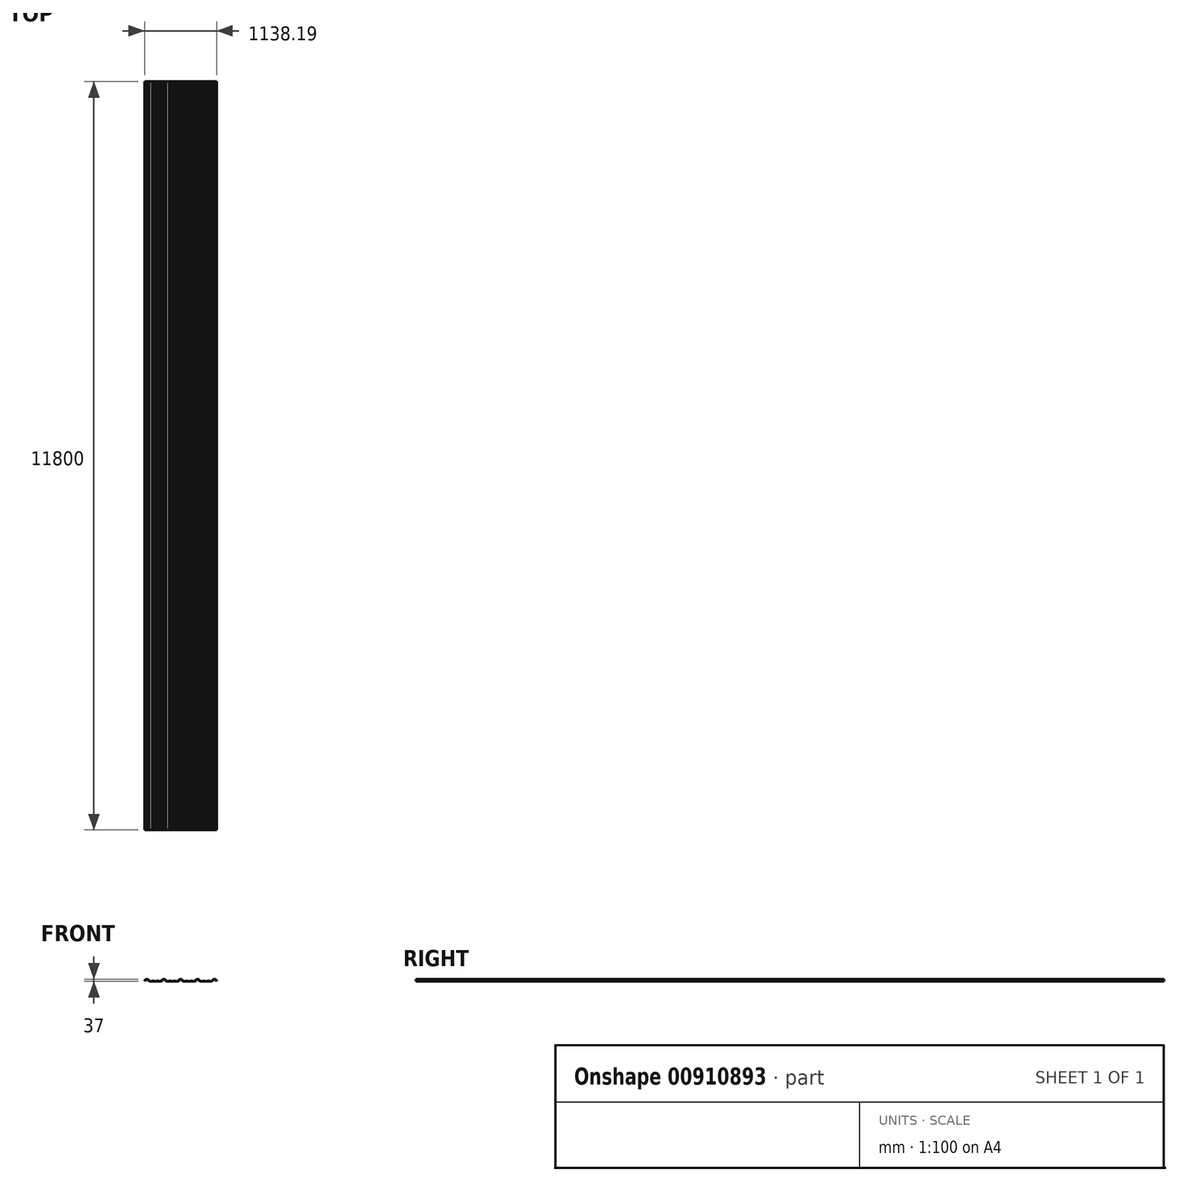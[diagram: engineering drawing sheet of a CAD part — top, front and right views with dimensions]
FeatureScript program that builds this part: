
annotation { "Feature Type Name" : "Feature", "Feature Type Description" : "" }
export const myFeature = defineFeature(function(context is Context, id is Id, definition is map)
    precondition{}
    {
        {
            var Q0;
            Q0=qCreatedBy(makeId("Front.planeOp"),FACE);
            var sketch = newSketch(context, id + "F0", { "sketchPlane" : qUnion([Q0])});
            skLineSegment(sketch, "E0.bottom", {"start": v(-37.5, 37) * mm, "end": v(37.5, 37) * mm, "construction": true});
            skLineSegment(sketch, "E0.top", {"start": v(-37.5, 0) * mm, "end": v(37.5, 0) * mm, "construction": true});
            skLineSegment(sketch, "E0.left", {"start": v(-37.5, 37) * mm, "end": v(-37.5, 0) * mm, "construction": true});
            skLineSegment(sketch, "E0.right", {"start": v(37.5, 37) * mm, "end": v(37.5, 0) * mm, "construction": true});
            skLineSegment(sketch, "E1.bottom", {"start": v(-16, 37) * mm, "end": v(16, 37) * mm, "construction": true});
            skLineSegment(sketch, "E1.top", {"start": v(-16, 0) * mm, "end": v(16, 0) * mm, "construction": true});
            skLineSegment(sketch, "E1.left", {"start": v(-16, 37) * mm, "end": v(-16, 0) * mm, "construction": true});
            skLineSegment(sketch, "E1.right", {"start": v(16, 37) * mm, "end": v(16, 0) * mm, "construction": true});
            skLineSegment(sketch, "E2.left", {"start": v(0, 37) * mm, "end": v(0, 0) * mm, "construction": true});
            skLineSegment(sketch, "E3", {"start": v(16, 37) * mm, "end": v(266, 37) * mm, "construction": true});
            skLineSegment(sketch, "E4", {"start": v(85.17, 0) * mm, "end": v(85.17, 6) * mm, "construction": true});
            skLineSegment(sketch, "E5", {"start": v(85.17, 3) * mm, "end": v(109.17, 3) * mm, "construction": true});
            skLineSegment(sketch, "E6", {"start": v(109.17, 3) * mm, "end": v(109.17, 0) * mm, "construction": true});
            skLineSegment(sketch, "E7", {"start": v(109.17, 0) * mm, "end": v(156.83, 0) * mm, "construction": true});
            skLineSegment(sketch, "E8", {"start": v(156.83, 0) * mm, "end": v(156.83, 3) * mm, "construction": true});
            skLineSegment(sketch, "E9", {"start": v(156.83, 3) * mm, "end": v(180.83, 3) * mm, "construction": true});
            skLineSegment(sketch, "E10", {"start": v(180.83, 3) * mm, "end": v(180.83, 0) * mm, "construction": true});
            skLineSegment(sketch, "E11", {"start": v(180.83, 0) * mm, "end": v(228.5, 0) * mm, "construction": true});
            skLineSegment(sketch, "E12", {"start": v(85.17, 0) * mm, "end": v(37.5, 0) * mm, "construction": true});
            skLineSegment(sketch, "E13", {"start": v(-37.5, 18.5) * mm, "end": v(37.5, 18.5) * mm, "construction": true});
            skLineSegment(sketch, "E14", {"start": v(-37.5, 3) * mm, "end": v(-28.55, 18.5) * mm, "construction": true});
            skLineSegment(sketch, "E15.0", {"start": v(-37.5, 15.5) * mm, "end": v(37.5, 15.5) * mm, "construction": true});
            skLineSegment(sketch, "E16.0", {"start": v(-37.5, 3) * mm, "end": v(37.5, 3) * mm, "construction": true});
            skLineSegment(sketch, "E17.0", {"start": v(-14.27, 34) * mm, "end": v(14.27, 34) * mm, "construction": true});
            skLineSegment(sketch, "E18.0", {"start": v(-35.77, 0) * mm, "end": v(-26.82, 15.5) * mm, "construction": true});
            skLineSegment(sketch, "E19", {"start": v(-26.68, 18.5) * mm, "end": v(-16, 37) * mm, "construction": true});
            skLineSegment(sketch, "E20.0", {"start": v(-24.95, 15.5) * mm, "end": v(-14.27, 34) * mm, "construction": true});
            skLineSegment(sketch, "E21.MirrorCS", {"start": v(37.5, 3) * mm, "end": v(28.55, 18.5) * mm, "construction": true});
            skLineSegment(sketch, "E22.MirrorCS", {"start": v(24.95, 15.5) * mm, "end": v(14.27, 34) * mm, "construction": true});
            skLineSegment(sketch, "E23.MirrorCS", {"start": v(35.77, 0) * mm, "end": v(26.82, 15.5) * mm, "construction": true});
            skLineSegment(sketch, "E24.MirrorCS", {"start": v(26.68, 18.5) * mm, "end": v(16, 37) * mm, "construction": true});
            skLineSegment(sketch, "E25.0", {"start": v(-36.7, 4.4) * mm, "end": v(-33.23, 4.4) * mm, "construction": true});
            skLineSegment(sketch, "E26.0", {"start": v(85.17, 3) * mm, "end": v(37.5, 3) * mm, "construction": true});
            skLineSegment(sketch, "E27.0", {"start": v(85.17, 6) * mm, "end": v(109.17, 6) * mm, "construction": true});
            skLineSegment(sketch, "E28.0", {"start": v(109.17, 3) * mm, "end": v(156.83, 3) * mm, "construction": true});
            skLineSegment(sketch, "E29.0", {"start": v(156.83, 6) * mm, "end": v(180.83, 6) * mm, "construction": true});
            skLineSegment(sketch, "E30.0", {"start": v(180.83, 3) * mm, "end": v(228.5, 3) * mm, "construction": true});
            skLineSegment(sketch, "E31", {"start": v(85.17, 0) * mm, "end": v(88.63, 6) * mm, "construction": true});
            skLineSegment(sketch, "E32", {"start": v(85.17, 6) * mm, "end": v(81.7, 0) * mm, "construction": true});
            skLineSegment(sketch, "E33", {"start": v(97.17, 6) * mm, "end": v(97.17, 3) * mm, "construction": true});
            skLineSegment(sketch, "E34.MirrorCS", {"start": v(109.17, 0) * mm, "end": v(105.7, 6) * mm, "construction": true});
            skLineSegment(sketch, "E35.MirrorCS", {"start": v(109.17, 6) * mm, "end": v(112.63, 0) * mm, "construction": true});
            skLineSegment(sketch, "E36", {"start": v(133, 3) * mm, "end": v(133, 0) * mm, "construction": true});
            skLineSegment(sketch, "E37.MirrorCS", {"start": v(156.83, 6) * mm, "end": v(153.37, 0) * mm, "construction": true});
            skLineSegment(sketch, "E38.MirrorCS", {"start": v(156.83, 0) * mm, "end": v(160.3, 6) * mm, "construction": true});
            skLineSegment(sketch, "E39.MirrorCS", {"start": v(168.83, 6) * mm, "end": v(168.83, 3) * mm, "construction": true});
            skLineSegment(sketch, "E40.MirrorCS", {"start": v(180.83, 0) * mm, "end": v(177.37, 6) * mm, "construction": true});
            skLineSegment(sketch, "E41.MirrorCS", {"start": v(180.83, 6) * mm, "end": v(184.3, 0) * mm, "construction": true});
            skLineSegment(sketch, "E42.1.0.0", {"start": v(228.5, 0) * mm, "end": v(303.5, 0) * mm, "construction": true});
            skLineSegment(sketch, "E42.1.0.1", {"start": v(250, 37) * mm, "end": v(250, 0) * mm, "construction": true});
            skLineSegment(sketch, "E42.1.0.2", {"start": v(292.68, 18.5) * mm, "end": v(282, 37) * mm, "construction": true});
            skLineSegment(sketch, "E42.1.0.3", {"start": v(241.05, 15.5) * mm, "end": v(251.73, 34) * mm, "construction": true});
            skLineSegment(sketch, "E42.1.0.4", {"start": v(228.5, 18.5) * mm, "end": v(303.5, 18.5) * mm, "construction": true});
            skLineSegment(sketch, "E42.1.0.5", {"start": v(303.5, 3) * mm, "end": v(294.55, 18.5) * mm, "construction": true});
            skLineSegment(sketch, "E42.1.0.6", {"start": v(228.5, 37) * mm, "end": v(303.5, 37) * mm, "construction": true});
            skLineSegment(sketch, "E42.1.0.7", {"start": v(301.77, 0) * mm, "end": v(292.82, 15.5) * mm, "construction": true});
            skLineSegment(sketch, "E42.1.0.8", {"start": v(303.5, 37) * mm, "end": v(303.5, 0) * mm, "construction": true});
            skLineSegment(sketch, "E42.1.0.9", {"start": v(446.83, 3) * mm, "end": v(494.5, 3) * mm, "construction": true});
            skLineSegment(sketch, "E42.1.0.10", {"start": v(290.95, 15.5) * mm, "end": v(280.27, 34) * mm, "construction": true});
            skLineSegment(sketch, "E42.1.0.11", {"start": v(266, 37) * mm, "end": v(266, 0) * mm, "construction": true});
            skLineSegment(sketch, "E42.1.0.12", {"start": v(250, 0) * mm, "end": v(282, 0) * mm, "construction": true});
            skLineSegment(sketch, "E42.1.0.13", {"start": v(228.5, 37) * mm, "end": v(228.5, 0) * mm, "construction": true});
            skLineSegment(sketch, "E42.1.0.14", {"start": v(228.5, 3) * mm, "end": v(303.5, 3) * mm, "construction": true});
            skLineSegment(sketch, "E42.1.0.15", {"start": v(351.17, 0) * mm, "end": v(303.5, 0) * mm, "construction": true});
            skLineSegment(sketch, "E42.1.0.16", {"start": v(351.17, 3) * mm, "end": v(303.5, 3) * mm, "construction": true});
            skLineSegment(sketch, "E42.1.0.17", {"start": v(228.5, 15.5) * mm, "end": v(303.5, 15.5) * mm, "construction": true});
            skLineSegment(sketch, "E42.1.0.18", {"start": v(282, 37) * mm, "end": v(282, 0) * mm, "construction": true});
            skLineSegment(sketch, "E42.1.0.19", {"start": v(375.17, 0) * mm, "end": v(422.83, 0) * mm, "construction": true});
            skLineSegment(sketch, "E42.1.0.20", {"start": v(446.83, 0) * mm, "end": v(494.5, 0) * mm, "construction": true});
            skLineSegment(sketch, "E42.1.0.21", {"start": v(375.17, 3) * mm, "end": v(422.83, 3) * mm, "construction": true});
            skLineSegment(sketch, "E42.1.0.22", {"start": v(250, 37) * mm, "end": v(282, 37) * mm, "construction": true});
            skLineSegment(sketch, "E42.1.0.23", {"start": v(239.32, 18.5) * mm, "end": v(250, 37) * mm, "construction": true});
            skLineSegment(sketch, "E42.1.0.24", {"start": v(351.17, 3) * mm, "end": v(375.17, 3) * mm, "construction": true});
            skLineSegment(sketch, "E42.1.0.25", {"start": v(251.73, 34) * mm, "end": v(280.27, 34) * mm, "construction": true});
            skLineSegment(sketch, "E42.1.0.26", {"start": v(228.5, 3) * mm, "end": v(237.45, 18.5) * mm, "construction": true});
            skLineSegment(sketch, "E42.1.0.27", {"start": v(351.17, 6) * mm, "end": v(375.17, 6) * mm, "construction": true});
            skLineSegment(sketch, "E42.1.0.28", {"start": v(230.23, 0) * mm, "end": v(239.18, 15.5) * mm, "construction": true});
            skLineSegment(sketch, "E42.1.0.29", {"start": v(434.83, 6) * mm, "end": v(434.83, 3) * mm, "construction": true});
            skLineSegment(sketch, "E42.1.0.30", {"start": v(363.17, 6) * mm, "end": v(363.17, 3) * mm, "construction": true});
            skLineSegment(sketch, "E42.1.0.31", {"start": v(422.83, 3) * mm, "end": v(446.83, 3) * mm, "construction": true});
            skLineSegment(sketch, "E42.1.0.32", {"start": v(229.3, 4.4) * mm, "end": v(232.77, 4.4) * mm, "construction": true});
            skLineSegment(sketch, "E42.1.0.33", {"start": v(422.83, 6) * mm, "end": v(446.83, 6) * mm, "construction": true});
            skLineSegment(sketch, "E42.1.0.34", {"start": v(399, 3) * mm, "end": v(399, 0) * mm, "construction": true});
            skLineSegment(sketch, "E42.1.0.35", {"start": v(446.83, 6) * mm, "end": v(450.3, 0) * mm, "construction": true});
            skLineSegment(sketch, "E42.1.0.36", {"start": v(422.83, 6) * mm, "end": v(419.37, 0) * mm, "construction": true});
            skLineSegment(sketch, "E42.1.0.37", {"start": v(375.17, 3) * mm, "end": v(375.17, 0) * mm, "construction": true});
            skLineSegment(sketch, "E42.1.0.38", {"start": v(446.83, 3) * mm, "end": v(446.83, 0) * mm, "construction": true});
            skLineSegment(sketch, "E42.1.0.39", {"start": v(446.83, 0) * mm, "end": v(443.37, 6) * mm, "construction": true});
            skLineSegment(sketch, "E42.1.0.40", {"start": v(375.17, 6) * mm, "end": v(378.63, 0) * mm, "construction": true});
            skLineSegment(sketch, "E42.1.0.41", {"start": v(422.83, 0) * mm, "end": v(426.3, 6) * mm, "construction": true});
            skLineSegment(sketch, "E42.1.0.42", {"start": v(375.17, 0) * mm, "end": v(371.7, 6) * mm, "construction": true});
            skLineSegment(sketch, "E42.1.0.43", {"start": v(351.17, 6) * mm, "end": v(347.7, 0) * mm, "construction": true});
            skLineSegment(sketch, "E42.1.0.44", {"start": v(422.83, 0) * mm, "end": v(422.83, 3) * mm, "construction": true});
            skLineSegment(sketch, "E42.1.0.45", {"start": v(351.17, 0) * mm, "end": v(351.17, 6) * mm, "construction": true});
            skLineSegment(sketch, "E42.1.0.46", {"start": v(351.17, 0) * mm, "end": v(354.63, 6) * mm, "construction": true});
            skLineSegment(sketch, "E42.2.0.0", {"start": v(494.5, 0) * mm, "end": v(569.5, 0) * mm, "construction": true});
            skLineSegment(sketch, "E42.2.0.1", {"start": v(516, 37) * mm, "end": v(516, 0) * mm, "construction": true});
            skLineSegment(sketch, "E42.2.0.2", {"start": v(558.68, 18.5) * mm, "end": v(548, 37) * mm, "construction": true});
            skLineSegment(sketch, "E42.2.0.3", {"start": v(507.05, 15.5) * mm, "end": v(517.73, 34) * mm, "construction": true});
            skLineSegment(sketch, "E42.2.0.4", {"start": v(494.5, 18.5) * mm, "end": v(569.5, 18.5) * mm, "construction": true});
            skLineSegment(sketch, "E42.2.0.5", {"start": v(569.5, 3) * mm, "end": v(560.55, 18.5) * mm, "construction": true});
            skLineSegment(sketch, "E42.2.0.6", {"start": v(494.5, 37) * mm, "end": v(569.5, 37) * mm, "construction": true});
            skLineSegment(sketch, "E42.2.0.7", {"start": v(567.77, 0) * mm, "end": v(558.82, 15.5) * mm, "construction": true});
            skLineSegment(sketch, "E42.2.0.8", {"start": v(569.5, 37) * mm, "end": v(569.5, 0) * mm, "construction": true});
            skLineSegment(sketch, "E42.2.0.9", {"start": v(712.83, 3) * mm, "end": v(760.5, 3) * mm, "construction": true});
            skLineSegment(sketch, "E42.2.0.10", {"start": v(556.95, 15.5) * mm, "end": v(546.27, 34) * mm, "construction": true});
            skLineSegment(sketch, "E42.2.0.11", {"start": v(532, 37) * mm, "end": v(532, 0) * mm, "construction": true});
            skLineSegment(sketch, "E42.2.0.12", {"start": v(516, 0) * mm, "end": v(548, 0) * mm, "construction": true});
            skLineSegment(sketch, "E42.2.0.13", {"start": v(494.5, 37) * mm, "end": v(494.5, 0) * mm, "construction": true});
            skLineSegment(sketch, "E42.2.0.14", {"start": v(494.5, 3) * mm, "end": v(569.5, 3) * mm, "construction": true});
            skLineSegment(sketch, "E42.2.0.15", {"start": v(617.17, 0) * mm, "end": v(569.5, 0) * mm, "construction": true});
            skLineSegment(sketch, "E42.2.0.16", {"start": v(617.17, 3) * mm, "end": v(569.5, 3) * mm, "construction": true});
            skLineSegment(sketch, "E42.2.0.17", {"start": v(494.5, 15.5) * mm, "end": v(569.5, 15.5) * mm, "construction": true});
            skLineSegment(sketch, "E42.2.0.18", {"start": v(548, 37) * mm, "end": v(548, 0) * mm, "construction": true});
            skLineSegment(sketch, "E42.2.0.19", {"start": v(641.17, 0) * mm, "end": v(688.83, 0) * mm, "construction": true});
            skLineSegment(sketch, "E42.2.0.20", {"start": v(712.83, 0) * mm, "end": v(760.5, 0) * mm, "construction": true});
            skLineSegment(sketch, "E42.2.0.21", {"start": v(641.17, 3) * mm, "end": v(688.83, 3) * mm, "construction": true});
            skLineSegment(sketch, "E42.2.0.22", {"start": v(516, 37) * mm, "end": v(548, 37) * mm, "construction": true});
            skLineSegment(sketch, "E42.2.0.23", {"start": v(505.32, 18.5) * mm, "end": v(516, 37) * mm, "construction": true});
            skLineSegment(sketch, "E42.2.0.24", {"start": v(617.17, 3) * mm, "end": v(641.17, 3) * mm, "construction": true});
            skLineSegment(sketch, "E42.2.0.25", {"start": v(517.73, 34) * mm, "end": v(546.27, 34) * mm, "construction": true});
            skLineSegment(sketch, "E42.2.0.26", {"start": v(494.5, 3) * mm, "end": v(503.45, 18.5) * mm, "construction": true});
            skLineSegment(sketch, "E42.2.0.27", {"start": v(617.17, 6) * mm, "end": v(641.17, 6) * mm, "construction": true});
            skLineSegment(sketch, "E42.2.0.28", {"start": v(496.23, 0) * mm, "end": v(505.18, 15.5) * mm, "construction": true});
            skLineSegment(sketch, "E42.2.0.29", {"start": v(700.83, 6) * mm, "end": v(700.83, 3) * mm, "construction": true});
            skLineSegment(sketch, "E42.2.0.30", {"start": v(629.17, 6) * mm, "end": v(629.17, 3) * mm, "construction": true});
            skLineSegment(sketch, "E42.2.0.31", {"start": v(688.83, 3) * mm, "end": v(712.83, 3) * mm, "construction": true});
            skLineSegment(sketch, "E42.2.0.32", {"start": v(495.3, 4.4) * mm, "end": v(498.77, 4.4) * mm, "construction": true});
            skLineSegment(sketch, "E42.2.0.33", {"start": v(688.83, 6) * mm, "end": v(712.83, 6) * mm, "construction": true});
            skLineSegment(sketch, "E42.2.0.34", {"start": v(665, 3) * mm, "end": v(665, 0) * mm, "construction": true});
            skLineSegment(sketch, "E42.2.0.35", {"start": v(712.83, 6) * mm, "end": v(716.3, 0) * mm, "construction": true});
            skLineSegment(sketch, "E42.2.0.36", {"start": v(688.83, 6) * mm, "end": v(685.37, 0) * mm, "construction": true});
            skLineSegment(sketch, "E42.2.0.37", {"start": v(641.17, 3) * mm, "end": v(641.17, 0) * mm, "construction": true});
            skLineSegment(sketch, "E42.2.0.38", {"start": v(712.83, 3) * mm, "end": v(712.83, 0) * mm, "construction": true});
            skLineSegment(sketch, "E42.2.0.39", {"start": v(712.83, 0) * mm, "end": v(709.37, 6) * mm, "construction": true});
            skLineSegment(sketch, "E42.2.0.40", {"start": v(641.17, 6) * mm, "end": v(644.63, 0) * mm, "construction": true});
            skLineSegment(sketch, "E42.2.0.41", {"start": v(688.83, 0) * mm, "end": v(692.3, 6) * mm, "construction": true});
            skLineSegment(sketch, "E42.2.0.42", {"start": v(641.17, 0) * mm, "end": v(637.7, 6) * mm, "construction": true});
            skLineSegment(sketch, "E42.2.0.43", {"start": v(617.17, 6) * mm, "end": v(613.7, 0) * mm, "construction": true});
            skLineSegment(sketch, "E42.2.0.44", {"start": v(688.83, 0) * mm, "end": v(688.83, 3) * mm, "construction": true});
            skLineSegment(sketch, "E42.2.0.45", {"start": v(617.17, 0) * mm, "end": v(617.17, 6) * mm, "construction": true});
            skLineSegment(sketch, "E42.2.0.46", {"start": v(617.17, 0) * mm, "end": v(620.63, 6) * mm, "construction": true});
            skLineSegment(sketch, "E42.3.0.0", {"start": v(760.5, 0) * mm, "end": v(835.5, 0) * mm, "construction": true});
            skLineSegment(sketch, "E42.3.0.1", {"start": v(782, 37) * mm, "end": v(782, 0) * mm, "construction": true});
            skLineSegment(sketch, "E42.3.0.2", {"start": v(824.68, 18.5) * mm, "end": v(814, 37) * mm, "construction": true});
            skLineSegment(sketch, "E42.3.0.3", {"start": v(773.05, 15.5) * mm, "end": v(783.73, 34) * mm, "construction": true});
            skLineSegment(sketch, "E42.3.0.4", {"start": v(760.5, 18.5) * mm, "end": v(835.5, 18.5) * mm, "construction": true});
            skLineSegment(sketch, "E42.3.0.5", {"start": v(835.5, 3) * mm, "end": v(826.55, 18.5) * mm, "construction": true});
            skLineSegment(sketch, "E42.3.0.6", {"start": v(760.5, 37) * mm, "end": v(835.5, 37) * mm, "construction": true});
            skLineSegment(sketch, "E42.3.0.7", {"start": v(833.77, 0) * mm, "end": v(824.82, 15.5) * mm, "construction": true});
            skLineSegment(sketch, "E42.3.0.8", {"start": v(835.5, 37) * mm, "end": v(835.5, 0) * mm, "construction": true});
            skLineSegment(sketch, "E42.3.0.9", {"start": v(978.83, 3) * mm, "end": v(1026.5, 3) * mm, "construction": true});
            skLineSegment(sketch, "E42.3.0.10", {"start": v(822.95, 15.5) * mm, "end": v(812.27, 34) * mm, "construction": true});
            skLineSegment(sketch, "E42.3.0.11", {"start": v(798, 37) * mm, "end": v(798, 0) * mm, "construction": true});
            skLineSegment(sketch, "E42.3.0.12", {"start": v(782, 0) * mm, "end": v(814, 0) * mm, "construction": true});
            skLineSegment(sketch, "E42.3.0.13", {"start": v(760.5, 37) * mm, "end": v(760.5, 0) * mm, "construction": true});
            skLineSegment(sketch, "E42.3.0.14", {"start": v(760.5, 3) * mm, "end": v(835.5, 3) * mm, "construction": true});
            skLineSegment(sketch, "E42.3.0.15", {"start": v(883.17, 0) * mm, "end": v(835.5, 0) * mm, "construction": true});
            skLineSegment(sketch, "E42.3.0.16", {"start": v(883.17, 3) * mm, "end": v(835.5, 3) * mm, "construction": true});
            skLineSegment(sketch, "E42.3.0.17", {"start": v(760.5, 15.5) * mm, "end": v(835.5, 15.5) * mm, "construction": true});
            skLineSegment(sketch, "E42.3.0.18", {"start": v(814, 37) * mm, "end": v(814, 0) * mm, "construction": true});
            skLineSegment(sketch, "E42.3.0.19", {"start": v(907.17, 0) * mm, "end": v(954.83, 0) * mm, "construction": true});
            skLineSegment(sketch, "E42.3.0.20", {"start": v(978.83, 0) * mm, "end": v(1026.5, 0) * mm, "construction": true});
            skLineSegment(sketch, "E42.3.0.21", {"start": v(907.17, 3) * mm, "end": v(954.83, 3) * mm, "construction": true});
            skLineSegment(sketch, "E42.3.0.22", {"start": v(782, 37) * mm, "end": v(814, 37) * mm, "construction": true});
            skLineSegment(sketch, "E42.3.0.23", {"start": v(771.32, 18.5) * mm, "end": v(782, 37) * mm, "construction": true});
            skLineSegment(sketch, "E42.3.0.24", {"start": v(883.17, 3) * mm, "end": v(907.17, 3) * mm, "construction": true});
            skLineSegment(sketch, "E42.3.0.25", {"start": v(783.73, 34) * mm, "end": v(812.27, 34) * mm, "construction": true});
            skLineSegment(sketch, "E42.3.0.26", {"start": v(760.5, 3) * mm, "end": v(769.45, 18.5) * mm, "construction": true});
            skLineSegment(sketch, "E42.3.0.27", {"start": v(883.17, 6) * mm, "end": v(907.17, 6) * mm, "construction": true});
            skLineSegment(sketch, "E42.3.0.28", {"start": v(762.23, 0) * mm, "end": v(771.18, 15.5) * mm, "construction": true});
            skLineSegment(sketch, "E42.3.0.29", {"start": v(966.83, 6) * mm, "end": v(966.83, 3) * mm, "construction": true});
            skLineSegment(sketch, "E42.3.0.30", {"start": v(895.17, 6) * mm, "end": v(895.17, 3) * mm, "construction": true});
            skLineSegment(sketch, "E42.3.0.31", {"start": v(954.83, 3) * mm, "end": v(978.83, 3) * mm, "construction": true});
            skLineSegment(sketch, "E42.3.0.32", {"start": v(761.3, 4.4) * mm, "end": v(764.77, 4.4) * mm, "construction": true});
            skLineSegment(sketch, "E42.3.0.33", {"start": v(954.83, 6) * mm, "end": v(978.83, 6) * mm, "construction": true});
            skLineSegment(sketch, "E42.3.0.34", {"start": v(931, 3) * mm, "end": v(931, 0) * mm, "construction": true});
            skLineSegment(sketch, "E42.3.0.35", {"start": v(978.83, 6) * mm, "end": v(982.3, 0) * mm, "construction": true});
            skLineSegment(sketch, "E42.3.0.36", {"start": v(954.83, 6) * mm, "end": v(951.37, 0) * mm, "construction": true});
            skLineSegment(sketch, "E42.3.0.37", {"start": v(907.17, 3) * mm, "end": v(907.17, 0) * mm, "construction": true});
            skLineSegment(sketch, "E42.3.0.38", {"start": v(978.83, 3) * mm, "end": v(978.83, 0) * mm, "construction": true});
            skLineSegment(sketch, "E42.3.0.39", {"start": v(978.83, 0) * mm, "end": v(975.37, 6) * mm, "construction": true});
            skLineSegment(sketch, "E42.3.0.40", {"start": v(907.17, 6) * mm, "end": v(910.63, 0) * mm, "construction": true});
            skLineSegment(sketch, "E42.3.0.41", {"start": v(954.83, 0) * mm, "end": v(958.3, 6) * mm, "construction": true});
            skLineSegment(sketch, "E42.3.0.42", {"start": v(907.17, 0) * mm, "end": v(903.7, 6) * mm, "construction": true});
            skLineSegment(sketch, "E42.3.0.43", {"start": v(883.17, 6) * mm, "end": v(879.7, 0) * mm, "construction": true});
            skLineSegment(sketch, "E42.3.0.44", {"start": v(954.83, 0) * mm, "end": v(954.83, 3) * mm, "construction": true});
            skLineSegment(sketch, "E42.3.0.45", {"start": v(883.17, 0) * mm, "end": v(883.17, 6) * mm, "construction": true});
            skLineSegment(sketch, "E42.3.0.46", {"start": v(883.17, 0) * mm, "end": v(886.63, 6) * mm, "construction": true});
            skLineSegment(sketch, "E42.4.0.0", {"start": v(1026.5, 0) * mm, "end": v(1101.5, 0) * mm, "construction": true});
            skLineSegment(sketch, "E42.4.0.1", {"start": v(1048, 37) * mm, "end": v(1048, 0) * mm, "construction": true});
            skLineSegment(sketch, "E42.4.0.2", {"start": v(1090.68, 18.5) * mm, "end": v(1080, 37) * mm, "construction": true});
            skLineSegment(sketch, "E42.4.0.3", {"start": v(1039.05, 15.5) * mm, "end": v(1049.73, 34) * mm, "construction": true});
            skLineSegment(sketch, "E42.4.0.4", {"start": v(1026.5, 18.5) * mm, "end": v(1101.5, 18.5) * mm, "construction": true});
            skLineSegment(sketch, "E42.4.0.5", {"start": v(1101.5, 3) * mm, "end": v(1092.55, 18.5) * mm, "construction": true});
            skLineSegment(sketch, "E42.4.0.6", {"start": v(1026.5, 37) * mm, "end": v(1101.5, 37) * mm, "construction": true});
            skLineSegment(sketch, "E42.4.0.7", {"start": v(1099.77, 0) * mm, "end": v(1090.82, 15.5) * mm, "construction": true});
            skLineSegment(sketch, "E42.4.0.8", {"start": v(1101.5, 37) * mm, "end": v(1101.5, 0) * mm, "construction": true});
            skLineSegment(sketch, "E42.4.0.9", {"start": v(1244.83, 3) * mm, "end": v(1292.5, 3) * mm, "construction": true});
            skLineSegment(sketch, "E42.4.0.10", {"start": v(1088.95, 15.5) * mm, "end": v(1078.27, 34) * mm, "construction": true});
            skLineSegment(sketch, "E42.4.0.11", {"start": v(1064, 37) * mm, "end": v(1064, 0) * mm, "construction": true});
            skLineSegment(sketch, "E42.4.0.12", {"start": v(1048, 0) * mm, "end": v(1080, 0) * mm, "construction": true});
            skLineSegment(sketch, "E42.4.0.13", {"start": v(1026.5, 37) * mm, "end": v(1026.5, 0) * mm, "construction": true});
            skLineSegment(sketch, "E42.4.0.14", {"start": v(1026.5, 3) * mm, "end": v(1101.5, 3) * mm, "construction": true});
            skLineSegment(sketch, "E42.4.0.15", {"start": v(1149.17, 0) * mm, "end": v(1101.5, 0) * mm, "construction": true});
            skLineSegment(sketch, "E42.4.0.16", {"start": v(1149.17, 3) * mm, "end": v(1101.5, 3) * mm, "construction": true});
            skLineSegment(sketch, "E42.4.0.17", {"start": v(1026.5, 15.5) * mm, "end": v(1101.5, 15.5) * mm, "construction": true});
            skLineSegment(sketch, "E42.4.0.18", {"start": v(1080, 37) * mm, "end": v(1080, 0) * mm, "construction": true});
            skLineSegment(sketch, "E42.4.0.19", {"start": v(1173.17, 0) * mm, "end": v(1220.83, 0) * mm, "construction": true});
            skLineSegment(sketch, "E42.4.0.20", {"start": v(1244.83, 0) * mm, "end": v(1292.5, 0) * mm, "construction": true});
            skLineSegment(sketch, "E42.4.0.21", {"start": v(1173.17, 3) * mm, "end": v(1220.83, 3) * mm, "construction": true});
            skLineSegment(sketch, "E42.4.0.22", {"start": v(1048, 37) * mm, "end": v(1080, 37) * mm, "construction": true});
            skLineSegment(sketch, "E42.4.0.23", {"start": v(1037.32, 18.5) * mm, "end": v(1048, 37) * mm, "construction": true});
            skLineSegment(sketch, "E42.4.0.24", {"start": v(1149.17, 3) * mm, "end": v(1173.17, 3) * mm, "construction": true});
            skLineSegment(sketch, "E42.4.0.25", {"start": v(1049.73, 34) * mm, "end": v(1078.27, 34) * mm, "construction": true});
            skLineSegment(sketch, "E42.4.0.26", {"start": v(1026.5, 3) * mm, "end": v(1035.45, 18.5) * mm, "construction": true});
            skLineSegment(sketch, "E42.4.0.27", {"start": v(1149.17, 6) * mm, "end": v(1173.17, 6) * mm, "construction": true});
            skLineSegment(sketch, "E42.4.0.28", {"start": v(1028.23, 0) * mm, "end": v(1037.18, 15.5) * mm, "construction": true});
            skLineSegment(sketch, "E42.4.0.29", {"start": v(1232.83, 6) * mm, "end": v(1232.83, 3) * mm, "construction": true});
            skLineSegment(sketch, "E42.4.0.30", {"start": v(1161.17, 6) * mm, "end": v(1161.17, 3) * mm, "construction": true});
            skLineSegment(sketch, "E42.4.0.31", {"start": v(1220.83, 3) * mm, "end": v(1244.83, 3) * mm, "construction": true});
            skLineSegment(sketch, "E42.4.0.32", {"start": v(1027.3, 4.4) * mm, "end": v(1030.77, 4.4) * mm, "construction": true});
            skLineSegment(sketch, "E42.4.0.33", {"start": v(1220.83, 6) * mm, "end": v(1244.83, 6) * mm, "construction": true});
            skLineSegment(sketch, "E42.4.0.34", {"start": v(1197, 3) * mm, "end": v(1197, 0) * mm, "construction": true});
            skLineSegment(sketch, "E42.4.0.35", {"start": v(1244.83, 6) * mm, "end": v(1248.3, 0) * mm, "construction": true});
            skLineSegment(sketch, "E42.4.0.36", {"start": v(1220.83, 6) * mm, "end": v(1217.37, 0) * mm, "construction": true});
            skLineSegment(sketch, "E42.4.0.37", {"start": v(1173.17, 3) * mm, "end": v(1173.17, 0) * mm, "construction": true});
            skLineSegment(sketch, "E42.4.0.38", {"start": v(1244.83, 3) * mm, "end": v(1244.83, 0) * mm, "construction": true});
            skLineSegment(sketch, "E42.4.0.39", {"start": v(1244.83, 0) * mm, "end": v(1241.37, 6) * mm, "construction": true});
            skLineSegment(sketch, "E42.4.0.40", {"start": v(1173.17, 6) * mm, "end": v(1176.63, 0) * mm, "construction": true});
            skLineSegment(sketch, "E42.4.0.41", {"start": v(1220.83, 0) * mm, "end": v(1224.3, 6) * mm, "construction": true});
            skLineSegment(sketch, "E42.4.0.42", {"start": v(1173.17, 0) * mm, "end": v(1169.7, 6) * mm, "construction": true});
            skLineSegment(sketch, "E42.4.0.43", {"start": v(1149.17, 6) * mm, "end": v(1145.7, 0) * mm, "construction": true});
            skLineSegment(sketch, "E42.4.0.44", {"start": v(1220.83, 0) * mm, "end": v(1220.83, 3) * mm, "construction": true});
            skLineSegment(sketch, "E42.4.0.45", {"start": v(1149.17, 0) * mm, "end": v(1149.17, 6) * mm, "construction": true});
            skLineSegment(sketch, "E42.4.0.46", {"start": v(1149.17, 0) * mm, "end": v(1152.63, 6) * mm, "construction": true});
            skLineSegment(sketch, "E42.direction1", {"start": v(-37.5, 0) * mm, "end": v(228.5, 0) * mm, "construction": true});
            skSolve(sketch);
        }
        {
            var Q0;
            Q0=qCreatedBy(makeId("Front.planeOp"),FACE);
            var sketch = newSketch(context, id + "F1", { "sketchPlane" : qUnion([Q0])});
            skLineSegment(sketch, "E43", {"start": v(-33.23, 4.4) * mm, "end": v(-36.7, 4.4) * mm});
            skLineSegment(sketch, "E44", {"start": v(-36.7, 4.4) * mm, "end": v(-28.55, 18.5) * mm});
            skLineSegment(sketch, "E45", {"start": v(-28.55, 18.5) * mm, "end": v(-26.68, 18.5) * mm});
            skLineSegment(sketch, "E46", {"start": v(-26.68, 18.5) * mm, "end": v(-16, 37) * mm});
            skLineSegment(sketch, "E47", {"start": v(-16, 37) * mm, "end": v(16, 37) * mm});
            skLineSegment(sketch, "E48", {"start": v(16, 37) * mm, "end": v(26.68, 18.5) * mm});
            skLineSegment(sketch, "E49", {"start": v(26.68, 18.5) * mm, "end": v(28.55, 18.5) * mm});
            skLineSegment(sketch, "E50", {"start": v(28.55, 18.5) * mm, "end": v(37.5, 3) * mm});
            skLineSegment(sketch, "E51", {"start": v(37.5, 3) * mm, "end": v(83.43, 3) * mm});
            skLineSegment(sketch, "E52", {"start": v(-33.23, 4.4) * mm, "end": v(-26.82, 15.5) * mm});
            skLineSegment(sketch, "E53", {"start": v(-26.82, 15.5) * mm, "end": v(-24.95, 15.5) * mm});
            skLineSegment(sketch, "E54", {"start": v(-24.95, 15.5) * mm, "end": v(-14.27, 34) * mm});
            skLineSegment(sketch, "E55", {"start": v(-14.27, 34) * mm, "end": v(14.27, 34) * mm});
            skLineSegment(sketch, "E56", {"start": v(14.27, 34) * mm, "end": v(24.95, 15.5) * mm});
            skLineSegment(sketch, "E57", {"start": v(24.95, 15.5) * mm, "end": v(26.82, 15.5) * mm});
            skLineSegment(sketch, "E58", {"start": v(26.82, 15.5) * mm, "end": v(35.77, 0) * mm});
            skLineSegment(sketch, "E59", {"start": v(35.77, 0) * mm, "end": v(85.17, 0) * mm});
            skLineSegment(sketch, "E60", {"start": v(83.43, 3) * mm, "end": v(85.17, 6) * mm});
            skLineSegment(sketch, "E61", {"start": v(85.17, 6) * mm, "end": v(109.17, 6) * mm});
            skLineSegment(sketch, "E62", {"start": v(109.17, 6) * mm, "end": v(110.9, 3) * mm});
            skLineSegment(sketch, "E63", {"start": v(110.9, 3) * mm, "end": v(155.1, 3) * mm});
            skLineSegment(sketch, "E64", {"start": v(155.1, 3) * mm, "end": v(156.83, 6) * mm});
            skLineSegment(sketch, "E65", {"start": v(156.83, 6) * mm, "end": v(180.83, 6) * mm});
            skLineSegment(sketch, "E66", {"start": v(85.17, 0) * mm, "end": v(86.9, 3) * mm});
            skLineSegment(sketch, "E67", {"start": v(86.9, 3) * mm, "end": v(107.43, 3) * mm});
            skLineSegment(sketch, "E68", {"start": v(107.43, 3) * mm, "end": v(109.17, 0) * mm});
            skLineSegment(sketch, "E69", {"start": v(109.17, 0) * mm, "end": v(156.83, 0) * mm});
            skLineSegment(sketch, "E70", {"start": v(156.83, 0) * mm, "end": v(158.57, 3) * mm});
            skLineSegment(sketch, "E71", {"start": v(158.57, 3) * mm, "end": v(179.1, 3) * mm});
            skLineSegment(sketch, "E72", {"start": v(179.1, 3) * mm, "end": v(180.83, 0) * mm});
            skLineSegment(sketch, "E73", {"start": v(180.83, 0) * mm, "end": v(230.23, 0) * mm});
            skLineSegment(sketch, "E74", {"start": v(230.23, 0) * mm, "end": v(239.18, 15.5) * mm});
            skLineSegment(sketch, "E75", {"start": v(239.18, 15.5) * mm, "end": v(241.05, 15.5) * mm});
            skLineSegment(sketch, "E76", {"start": v(241.05, 15.5) * mm, "end": v(251.73, 34) * mm});
            skLineSegment(sketch, "E77", {"start": v(251.73, 34) * mm, "end": v(280.27, 34) * mm});
            skLineSegment(sketch, "E78", {"start": v(280.27, 34) * mm, "end": v(290.95, 15.5) * mm});
            skLineSegment(sketch, "E79", {"start": v(290.95, 15.5) * mm, "end": v(292.82, 15.5) * mm});
            skLineSegment(sketch, "E80", {"start": v(292.82, 15.5) * mm, "end": v(301.77, 0) * mm});
            skLineSegment(sketch, "E81", {"start": v(180.83, 6) * mm, "end": v(182.57, 3) * mm});
            skLineSegment(sketch, "E82", {"start": v(182.57, 3) * mm, "end": v(228.5, 3) * mm});
            skLineSegment(sketch, "E83", {"start": v(228.5, 3) * mm, "end": v(237.45, 18.5) * mm});
            skLineSegment(sketch, "E84", {"start": v(237.45, 18.5) * mm, "end": v(239.32, 18.5) * mm});
            skLineSegment(sketch, "E85", {"start": v(239.32, 18.5) * mm, "end": v(250, 37) * mm});
            skLineSegment(sketch, "E86", {"start": v(250, 37) * mm, "end": v(282, 37) * mm});
            skLineSegment(sketch, "E87", {"start": v(282, 37) * mm, "end": v(292.68, 18.5) * mm});
            skLineSegment(sketch, "E88", {"start": v(292.68, 18.5) * mm, "end": v(294.55, 18.5) * mm});
            skLineSegment(sketch, "E89", {"start": v(294.55, 18.5) * mm, "end": v(303.5, 3) * mm});
            skLineSegment(sketch, "E90.1.0.0", {"start": v(375.17, 0) * mm, "end": v(422.83, 0) * mm});
            skLineSegment(sketch, "E90.1.0.1", {"start": v(546.27, 34) * mm, "end": v(556.95, 15.5) * mm});
            skLineSegment(sketch, "E90.1.0.2", {"start": v(558.82, 15.5) * mm, "end": v(567.77, 0) * mm});
            skLineSegment(sketch, "E90.1.0.3", {"start": v(303.5, 3) * mm, "end": v(349.43, 3) * mm});
            skLineSegment(sketch, "E90.1.0.4", {"start": v(448.57, 3) * mm, "end": v(494.5, 3) * mm});
            skLineSegment(sketch, "E90.1.0.5", {"start": v(301.77, 0) * mm, "end": v(351.17, 0) * mm});
            skLineSegment(sketch, "E90.1.0.6", {"start": v(351.17, 6) * mm, "end": v(375.17, 6) * mm});
            skLineSegment(sketch, "E90.1.0.7", {"start": v(517.73, 34) * mm, "end": v(546.27, 34) * mm});
            skLineSegment(sketch, "E90.1.0.8", {"start": v(507.05, 15.5) * mm, "end": v(517.73, 34) * mm});
            skLineSegment(sketch, "E90.1.0.9", {"start": v(446.83, 0) * mm, "end": v(496.23, 0) * mm});
            skLineSegment(sketch, "E90.1.0.10", {"start": v(352.9, 3) * mm, "end": v(373.43, 3) * mm});
            skLineSegment(sketch, "E90.1.0.11", {"start": v(376.9, 3) * mm, "end": v(421.1, 3) * mm});
            skLineSegment(sketch, "E90.1.0.12", {"start": v(494.5, 3) * mm, "end": v(503.45, 18.5) * mm});
            skLineSegment(sketch, "E90.1.0.13", {"start": v(505.32, 18.5) * mm, "end": v(516, 37) * mm});
            skLineSegment(sketch, "E90.1.0.14", {"start": v(548, 37) * mm, "end": v(558.68, 18.5) * mm});
            skLineSegment(sketch, "E90.1.0.15", {"start": v(424.57, 3) * mm, "end": v(445.1, 3) * mm});
            skLineSegment(sketch, "E90.1.0.16", {"start": v(496.23, 0) * mm, "end": v(505.18, 15.5) * mm});
            skLineSegment(sketch, "E90.1.0.17", {"start": v(560.55, 18.5) * mm, "end": v(569.5, 3) * mm});
            skLineSegment(sketch, "E90.1.0.18", {"start": v(422.83, 6) * mm, "end": v(446.83, 6) * mm});
            skLineSegment(sketch, "E90.1.0.19", {"start": v(516, 37) * mm, "end": v(548, 37) * mm});
            skLineSegment(sketch, "E90.1.0.20", {"start": v(375.17, 6) * mm, "end": v(376.9, 3) * mm});
            skLineSegment(sketch, "E90.1.0.21", {"start": v(503.45, 18.5) * mm, "end": v(505.32, 18.5) * mm});
            skLineSegment(sketch, "E90.1.0.22", {"start": v(421.1, 3) * mm, "end": v(422.83, 6) * mm});
            skLineSegment(sketch, "E90.1.0.23", {"start": v(558.68, 18.5) * mm, "end": v(560.55, 18.5) * mm});
            skLineSegment(sketch, "E90.1.0.24", {"start": v(556.95, 15.5) * mm, "end": v(558.82, 15.5) * mm});
            skLineSegment(sketch, "E90.1.0.25", {"start": v(445.1, 3) * mm, "end": v(446.83, 0) * mm});
            skLineSegment(sketch, "E90.1.0.26", {"start": v(349.43, 3) * mm, "end": v(351.17, 6) * mm});
            skLineSegment(sketch, "E90.1.0.27", {"start": v(446.83, 6) * mm, "end": v(448.57, 3) * mm});
            skLineSegment(sketch, "E90.1.0.28", {"start": v(351.17, 0) * mm, "end": v(352.9, 3) * mm});
            skLineSegment(sketch, "E90.1.0.29", {"start": v(505.18, 15.5) * mm, "end": v(507.05, 15.5) * mm});
            skLineSegment(sketch, "E90.1.0.30", {"start": v(422.83, 0) * mm, "end": v(424.57, 3) * mm});
            skLineSegment(sketch, "E90.1.0.31", {"start": v(373.43, 3) * mm, "end": v(375.17, 0) * mm});
            skLineSegment(sketch, "E90.2.0.0", {"start": v(641.17, 0) * mm, "end": v(688.83, 0) * mm});
            skLineSegment(sketch, "E90.2.0.1", {"start": v(812.27, 34) * mm, "end": v(822.95, 15.5) * mm});
            skLineSegment(sketch, "E90.2.0.2", {"start": v(824.82, 15.5) * mm, "end": v(833.77, 0) * mm});
            skLineSegment(sketch, "E90.2.0.3", {"start": v(569.5, 3) * mm, "end": v(615.43, 3) * mm});
            skLineSegment(sketch, "E90.2.0.4", {"start": v(714.57, 3) * mm, "end": v(760.5, 3) * mm});
            skLineSegment(sketch, "E90.2.0.5", {"start": v(567.77, 0) * mm, "end": v(617.17, 0) * mm});
            skLineSegment(sketch, "E90.2.0.6", {"start": v(617.17, 6) * mm, "end": v(641.17, 6) * mm});
            skLineSegment(sketch, "E90.2.0.7", {"start": v(783.73, 34) * mm, "end": v(812.27, 34) * mm});
            skLineSegment(sketch, "E90.2.0.8", {"start": v(773.05, 15.5) * mm, "end": v(783.73, 34) * mm});
            skLineSegment(sketch, "E90.2.0.9", {"start": v(712.83, 0) * mm, "end": v(762.23, 0) * mm});
            skLineSegment(sketch, "E90.2.0.10", {"start": v(618.9, 3) * mm, "end": v(639.43, 3) * mm});
            skLineSegment(sketch, "E90.2.0.11", {"start": v(642.9, 3) * mm, "end": v(687.1, 3) * mm});
            skLineSegment(sketch, "E90.2.0.12", {"start": v(760.5, 3) * mm, "end": v(769.45, 18.5) * mm});
            skLineSegment(sketch, "E90.2.0.13", {"start": v(771.32, 18.5) * mm, "end": v(782, 37) * mm});
            skLineSegment(sketch, "E90.2.0.14", {"start": v(814, 37) * mm, "end": v(824.68, 18.5) * mm});
            skLineSegment(sketch, "E90.2.0.15", {"start": v(690.57, 3) * mm, "end": v(711.1, 3) * mm});
            skLineSegment(sketch, "E90.2.0.16", {"start": v(762.23, 0) * mm, "end": v(771.18, 15.5) * mm});
            skLineSegment(sketch, "E90.2.0.17", {"start": v(826.55, 18.5) * mm, "end": v(835.5, 3) * mm});
            skLineSegment(sketch, "E90.2.0.18", {"start": v(688.83, 6) * mm, "end": v(712.83, 6) * mm});
            skLineSegment(sketch, "E90.2.0.19", {"start": v(782, 37) * mm, "end": v(814, 37) * mm});
            skLineSegment(sketch, "E90.2.0.20", {"start": v(641.17, 6) * mm, "end": v(642.9, 3) * mm});
            skLineSegment(sketch, "E90.2.0.21", {"start": v(769.45, 18.5) * mm, "end": v(771.32, 18.5) * mm});
            skLineSegment(sketch, "E90.2.0.22", {"start": v(687.1, 3) * mm, "end": v(688.83, 6) * mm});
            skLineSegment(sketch, "E90.2.0.23", {"start": v(824.68, 18.5) * mm, "end": v(826.55, 18.5) * mm});
            skLineSegment(sketch, "E90.2.0.24", {"start": v(822.95, 15.5) * mm, "end": v(824.82, 15.5) * mm});
            skLineSegment(sketch, "E90.2.0.25", {"start": v(711.1, 3) * mm, "end": v(712.83, 0) * mm});
            skLineSegment(sketch, "E90.2.0.26", {"start": v(615.43, 3) * mm, "end": v(617.17, 6) * mm});
            skLineSegment(sketch, "E90.2.0.27", {"start": v(712.83, 6) * mm, "end": v(714.57, 3) * mm});
            skLineSegment(sketch, "E90.2.0.28", {"start": v(617.17, 0) * mm, "end": v(618.9, 3) * mm});
            skLineSegment(sketch, "E90.2.0.29", {"start": v(771.18, 15.5) * mm, "end": v(773.05, 15.5) * mm});
            skLineSegment(sketch, "E90.2.0.30", {"start": v(688.83, 0) * mm, "end": v(690.57, 3) * mm});
            skLineSegment(sketch, "E90.2.0.31", {"start": v(639.43, 3) * mm, "end": v(641.17, 0) * mm});
            skLineSegment(sketch, "E90.3.0.0", {"start": v(907.17, 0) * mm, "end": v(954.83, 0) * mm});
            skLineSegment(sketch, "E90.3.0.1", {"start": v(1078.27, 34) * mm, "end": v(1088.95, 15.5) * mm});
            skLineSegment(sketch, "E90.3.0.2", {"start": v(1090.82, 15.5) * mm, "end": v(1099.77, 0) * mm});
            skLineSegment(sketch, "E90.3.0.3", {"start": v(835.5, 3) * mm, "end": v(881.43, 3) * mm});
            skLineSegment(sketch, "E90.3.0.4", {"start": v(980.57, 3) * mm, "end": v(1026.5, 3) * mm});
            skLineSegment(sketch, "E90.3.0.5", {"start": v(833.77, 0) * mm, "end": v(883.17, 0) * mm});
            skLineSegment(sketch, "E90.3.0.6", {"start": v(883.17, 6) * mm, "end": v(907.17, 6) * mm});
            skLineSegment(sketch, "E90.3.0.7", {"start": v(1049.73, 34) * mm, "end": v(1078.27, 34) * mm});
            skLineSegment(sketch, "E90.3.0.8", {"start": v(1039.05, 15.5) * mm, "end": v(1049.73, 34) * mm});
            skLineSegment(sketch, "E90.3.0.9", {"start": v(978.83, 0) * mm, "end": v(1028.23, 0) * mm});
            skLineSegment(sketch, "E90.3.0.10", {"start": v(884.9, 3) * mm, "end": v(905.43, 3) * mm});
            skLineSegment(sketch, "E90.3.0.11", {"start": v(908.9, 3) * mm, "end": v(953.1, 3) * mm});
            skLineSegment(sketch, "E90.3.0.12", {"start": v(1026.5, 3) * mm, "end": v(1035.45, 18.5) * mm});
            skLineSegment(sketch, "E90.3.0.13", {"start": v(1037.32, 18.5) * mm, "end": v(1048, 37) * mm});
            skLineSegment(sketch, "E90.3.0.14", {"start": v(1080, 37) * mm, "end": v(1090.68, 18.5) * mm});
            skLineSegment(sketch, "E90.3.0.15", {"start": v(956.57, 3) * mm, "end": v(977.1, 3) * mm});
            skLineSegment(sketch, "E90.3.0.16", {"start": v(1028.23, 0) * mm, "end": v(1037.18, 15.5) * mm});
            skLineSegment(sketch, "E90.3.0.17", {"start": v(1092.55, 18.5) * mm, "end": v(1101.5, 3) * mm});
            skLineSegment(sketch, "E90.3.0.18", {"start": v(954.83, 6) * mm, "end": v(978.83, 6) * mm});
            skLineSegment(sketch, "E90.3.0.19", {"start": v(1048, 37) * mm, "end": v(1080, 37) * mm});
            skLineSegment(sketch, "E90.3.0.20", {"start": v(907.17, 6) * mm, "end": v(908.9, 3) * mm});
            skLineSegment(sketch, "E90.3.0.21", {"start": v(1035.45, 18.5) * mm, "end": v(1037.32, 18.5) * mm});
            skLineSegment(sketch, "E90.3.0.22", {"start": v(953.1, 3) * mm, "end": v(954.83, 6) * mm});
            skLineSegment(sketch, "E90.3.0.23", {"start": v(1090.68, 18.5) * mm, "end": v(1092.55, 18.5) * mm});
            skLineSegment(sketch, "E90.3.0.24", {"start": v(1088.95, 15.5) * mm, "end": v(1090.82, 15.5) * mm});
            skLineSegment(sketch, "E90.3.0.25", {"start": v(977.1, 3) * mm, "end": v(978.83, 0) * mm});
            skLineSegment(sketch, "E90.3.0.26", {"start": v(881.43, 3) * mm, "end": v(883.17, 6) * mm});
            skLineSegment(sketch, "E90.3.0.27", {"start": v(978.83, 6) * mm, "end": v(980.57, 3) * mm});
            skLineSegment(sketch, "E90.3.0.28", {"start": v(883.17, 0) * mm, "end": v(884.9, 3) * mm});
            skLineSegment(sketch, "E90.3.0.29", {"start": v(1037.18, 15.5) * mm, "end": v(1039.05, 15.5) * mm});
            skLineSegment(sketch, "E90.3.0.30", {"start": v(954.83, 0) * mm, "end": v(956.57, 3) * mm});
            skLineSegment(sketch, "E90.3.0.31", {"start": v(905.43, 3) * mm, "end": v(907.17, 0) * mm});
            skLineSegment(sketch, "E90.direction1", {"start": v(35.77, 0) * mm, "end": v(301.77, 0) * mm, "construction": true});
            skLineSegment(sketch, "E91", {"start": v(1101.5, 3) * mm, "end": v(1099.77, 0) * mm});
            skSolve(sketch);
        }
        {
            var Q0;
            Q0=makeQuery(id+"F1.imprint","IMPRINT",FACE,{"disambiguationData":[TD([[makeQuery(id+"F1.imprint","IMPRINT",EDGE,{"derivedFrom":sQuery(id+"F1.wireOp",EDGE,"E43")}),-1.0]])]});
            extrude(context, id + "F2", {"entities" : qUnion([Q0]), "depth" : 11800 * mm, "offsetDistance" : 25 * mm});
        }
    });
